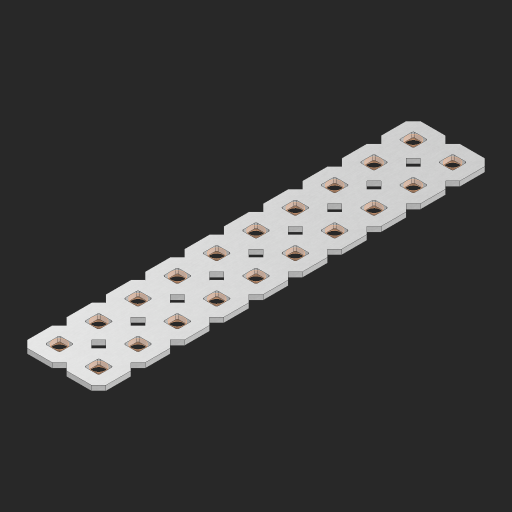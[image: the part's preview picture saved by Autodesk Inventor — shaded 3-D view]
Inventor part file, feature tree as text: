
AUTODESK INVENTOR PART (.ipt)
format: ipt  version: 2023 (Build 270158000, 158)  size: 506,880 bytes
history: native  units: in
note: dims shown in document units (in); Inventor stores cm internally (conversion verified against a paired STEP export)
features: other x21, extrude x19, sketch x2, pattern_linear x1
ambient origin geometry x8: Origin, YZ Plane, XZ Plane, XY Plane, X Axis, Y Axis, Z Axis, Center Point
bodies: Solid1 (feature_tree), Body (feature_tree)
feature tree (43):
  pattern_linear  "Rectangular Pattern1"  Spacing1=0.09in  [1 undecoded]
  sketch  "Sketch1"  dims[d1=0.5in]
  sketch  "Sketch2"  dims[d2=0.182in d3=0.09in d4=0.09in d5=0.09in d6=0.09in d7=0.09in d8=0.09in d9=0.09in d10=0.09in d11=0.02in d13=0.0in d14=0.172in d15=0.0625in d16=0.0in d19=0.5in d22=0.5in]
  other  "Srf1"
  other  "Srf126"
  other  "Srf127"
  other  "Srf128"
  other  "Srf129"
  other  "Srf130"
  other  "Srf131"
  other  "Srf250"
  other  "Srf251"
  other  "Srf252"
  other  "Srf268"
  other  "Srf269"
  other  "Srf270"
  other  "Srf271"
  other  "Srf272"
  other  "Srf273"
  other  "Srf274"
  other  "Srf275"
  other  "Srf276"
  other  "Srf277"
  other  "Circle"
  extrude  "ExtrusionSrf126"  Depth=0.09in
  extrude  "ExtrusionSrf127"  Depth=0.09in
  extrude  "ExtrusionSrf128"  Depth=0.09in
  extrude  "ExtrusionSrf129"  Depth=0.09in
  extrude  "ExtrusionSrf130"  Depth=0.09in
  extrude  "ExtrusionSrf131"  Depth=0.09in
  extrude  "ExtrusionSrf250"  Depth=0.09in
  extrude  "ExtrusionSrf251"  Depth=0.02in
  extrude  "ExtrusionSrf252"  TaperAngle=0.0deg  [1 undecoded]
  extrude  "ExtrusionSrf268"  Depth=0.5in
  extrude  "ExtrusionSrf269"  Depth=0.0625in TaperAngle=0.0deg
  extrude  "ExtrusionSrf270"  Depth=0.5in
  extrude  "ExtrusionSrf271"  Depth=0.5in
  extrude  "ExtrusionSrf272"  [1 undecoded]
  extrude  "ExtrusionSrf273"  [1 undecoded]
  extrude  "ExtrusionSrf274"  [1 undecoded]
  extrude  "ExtrusionSrf275"  [1 undecoded]
  extrude  "ExtrusionSrf276"  [1 undecoded]
  extrude  "ExtrusionSrf277"  [1 undecoded]
note: 8 required parameter values undecoded (feature->parameter linkage not recoverable at this tier; creation-order binding heuristic only, values carry confidence <= 0.55)
